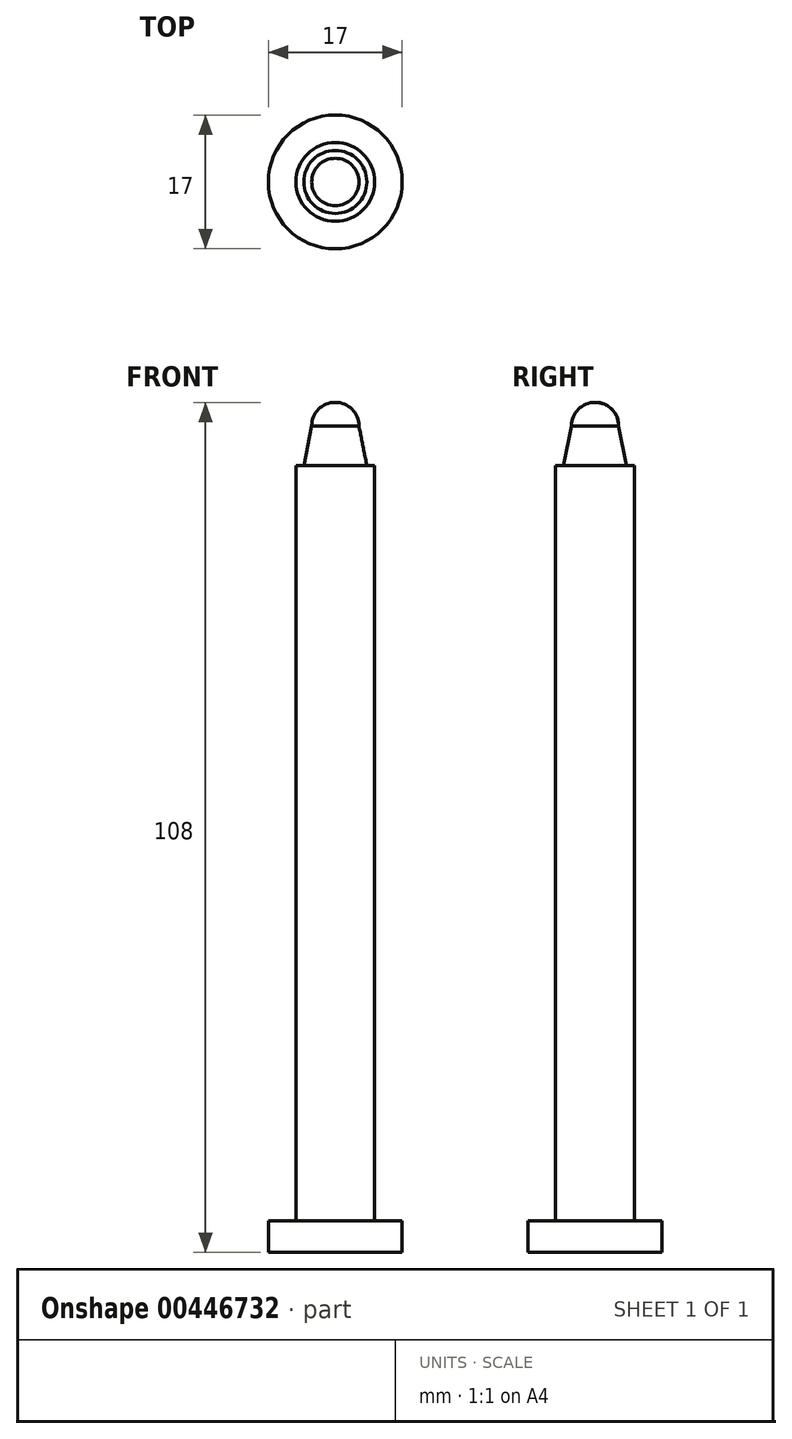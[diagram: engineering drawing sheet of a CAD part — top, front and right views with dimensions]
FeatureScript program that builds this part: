
annotation { "Feature Type Name" : "Feature", "Feature Type Description" : "" }
export const myFeature = defineFeature(function(context is Context, id is Id, definition is map)
    precondition{}
    {
        {
            var Q0;
            Q0=qCreatedBy(makeId("Top.planeOp"),FACE);
            var sketch = newSketch(context, id + "F0", { "sketchPlane" : qUnion([Q0])});
            skCircle(sketch, "E0", {"center": v(0, 0) * mm, "radius": 8.5 * mm});
            skSolve(sketch);
        }
        {
            var Q0;
            Q0=qSketchRegion(id+"F0",true);
            extrude(context, id + "F1", {"entities" : qUnion([Q0]), "depth" : 4 * mm});
        }
        {
            var Q0;
            Q0=qCreatedBy(makeId("Top.planeOp"),FACE);
            var sketch = newSketch(context, id + "F2", { "sketchPlane" : qUnion([Q0])});
            skCircle(sketch, "E1", {"center": v(0, 0) * mm, "radius": 5 * mm});
            skSolve(sketch);
        }
        {
            var Q0;
            Q0=qSketchRegion(id+"F2",true);
            extrude(context, id + "F3", {"entities" : qUnion([Q0]), "operationType" : NewBodyOperationType.ADD, "depth" : 100 * mm});
        }
        {
            var Q0;
            Q0=qCreatedBy(makeId("Right.planeOp"),FACE);
            var sketch = newSketch(context, id + "F4", { "sketchPlane" : qUnion([Q0])});
            skLineSegment(sketch, "E2", {"start": v(0, 105) * mm, "end": v(0, 100) * mm});
            skLineSegment(sketch, "E3", {"start": v(0, 100) * mm, "end": v(4, 100) * mm});
            skLineSegment(sketch, "E4", {"start": v(4, 100) * mm, "end": v(3, 105) * mm});
            skLineSegment(sketch, "E5", {"start": v(3, 105) * mm, "end": v(0, 105) * mm});
            skSolve(sketch);
        }
        {
            var Q0;
            Q0=makeQuery(id+"F4.imprint","IMPRINT",FACE,{"disambiguationData":[TD([[makeQuery(id+"F4.imprint","IMPRINT",EDGE,{"derivedFrom":sQuery(id+"F4.wireOp",EDGE,"E2")}),1.0]])]});
            var Q1;
            Q1=sQuery(id+"F4.wireOp",EDGE,"E2");
            revolve(context, id + "F5", {"operationType" : NewBodyOperationType.ADD, "entities" : qUnion([Q0]), "axis" : qUnion([Q1]), "revolveType" : RevolveType.FULL});
        }
        {
            var Q0;
            Q0=qCreatedBy(makeId("Right.planeOp"),FACE);
            var sketch = newSketch(context, id + "F6", { "sketchPlane" : qUnion([Q0])});
            skLineSegment(sketch, "E6", {"start": v(0, 108) * mm, "end": v(0, 105) * mm});
            skLineSegment(sketch, "E7", {"start": v(0, 105) * mm, "end": v(3, 105) * mm});
            skArc(sketch, "E8", {"start": v(3, 105) * mm, "mid": v(2.12, 107.12) * mm, "end": v(0, 108) * mm});
            skSolve(sketch);
        }
        {
            var Q0;
            Q0=makeQuery(id+"F6.imprint","IMPRINT",FACE,{"disambiguationData":[TD([[makeQuery(id+"F6.imprint","IMPRINT",EDGE,{"derivedFrom":sQuery(id+"F6.wireOp",EDGE,"E6")}),1.0]])]});
            var Q1;
            Q1=sQuery(id+"F6.wireOp",EDGE,"E6");
            revolve(context, id + "F7", {"operationType" : NewBodyOperationType.ADD, "entities" : qUnion([Q0]), "axis" : qUnion([Q1]), "revolveType" : RevolveType.FULL});
        }
    });
